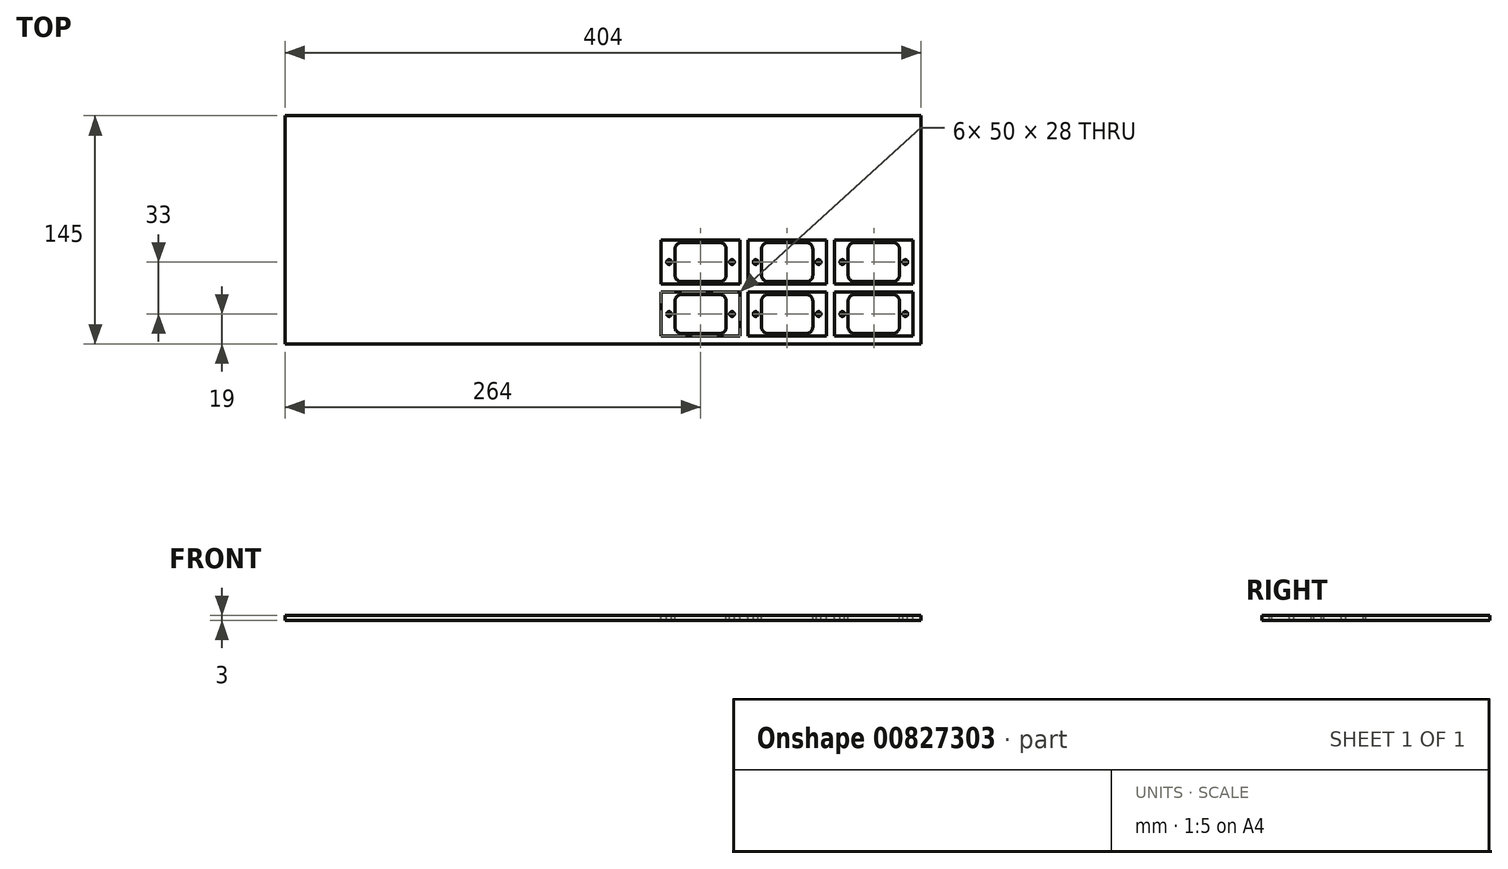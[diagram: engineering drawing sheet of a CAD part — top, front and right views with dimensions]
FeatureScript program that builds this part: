
annotation { "Feature Type Name" : "Feature", "Feature Type Description" : "" }
export const myFeature = defineFeature(function(context is Context, id is Id, definition is map)
    precondition{}
    {
        {
            var Q0;
            Q0=qCreatedBy(makeId("Top.planeOp"),FACE);
            var sketch = newSketch(context, id + "F0", { "sketchPlane" : qUnion([Q0])});
            skLineSegment(sketch, "E0.bottom", {"start": v(202, 72.5) * mm, "end": v(-202, 72.5) * mm});
            skLineSegment(sketch, "E0.top", {"start": v(202, -72.5) * mm, "end": v(-202, -72.5) * mm});
            skLineSegment(sketch, "E0.left", {"start": v(202, 72.5) * mm, "end": v(202, -72.5) * mm});
            skLineSegment(sketch, "E0.right", {"start": v(-202, 72.5) * mm, "end": v(-202, -72.5) * mm});
            skPoint(sketch, "E0.middle", {"position": v(0, 0) * mm});
            skSolve(sketch);
        }
        {
            var Q0;
            Q0=qCreatedBy(makeId("Top.planeOp"),FACE);
            var sketch = newSketch(context, id + "F1", { "sketchPlane" : qUnion([Q0])});
            skLineSegment(sketch, "E1.bottom", {"start": v(184.25, -65.9) * mm, "end": v(159.75, -65.9) * mm});
            skLineSegment(sketch, "E1.top", {"start": v(184.25, -41.1) * mm, "end": v(159.75, -41.1) * mm});
            skLineSegment(sketch, "E1.left", {"start": v(188.25, -61.9) * mm, "end": v(188.25, -45.1) * mm});
            skLineSegment(sketch, "E1.right", {"start": v(155.75, -61.9) * mm, "end": v(155.75, -45.1) * mm});
            skPoint(sketch, "E1.middle", {"position": v(172, -53.5) * mm});
            skPoint(sketch, "E2.visualSharp", {"position": v(155.75, -41.1) * mm});
            skArc(sketch, "E2.filletArc", {"start": v(159.75, -41.1) * mm, "mid": v(156.92, -42.27) * mm, "end": v(155.75, -45.1) * mm});
            skPoint(sketch, "E3.visualSharp", {"position": v(188.25, -41.1) * mm});
            skArc(sketch, "E3.filletArc", {"start": v(188.25, -45.1) * mm, "mid": v(187.08, -42.27) * mm, "end": v(184.25, -41.1) * mm});
            skPoint(sketch, "E4.visualSharp", {"position": v(188.25, -65.9) * mm});
            skArc(sketch, "E4.filletArc", {"start": v(184.25, -65.9) * mm, "mid": v(187.08, -64.73) * mm, "end": v(188.25, -61.9) * mm});
            skPoint(sketch, "E5.visualSharp", {"position": v(155.75, -65.9) * mm});
            skArc(sketch, "E5.filletArc", {"start": v(155.75, -61.9) * mm, "mid": v(156.92, -64.73) * mm, "end": v(159.75, -65.9) * mm});
            skCircle(sketch, "E6", {"center": v(192, -53.5) * mm, "radius": 1.5 * mm});
            skCircle(sketch, "E7", {"center": v(152, -53.5) * mm, "radius": 1.5 * mm});
            skLineSegment(sketch, "E8", {"start": v(147, -39.5) * mm, "end": v(147, -67.5) * mm});
            skLineSegment(sketch, "E9", {"start": v(147, -67.5) * mm, "end": v(197, -67.5) * mm});
            skLineSegment(sketch, "E10", {"start": v(197, -67.5) * mm, "end": v(197, -39.5) * mm});
            skLineSegment(sketch, "E11", {"start": v(197, -39.5) * mm, "end": v(147, -39.5) * mm});
            skLineSegment(sketch, "E12.0.1.0", {"start": v(184.25, -32.9) * mm, "end": v(159.75, -32.9) * mm});
            skLineSegment(sketch, "E12.0.1.1", {"start": v(184.25, -8.1) * mm, "end": v(159.75, -8.1) * mm});
            skLineSegment(sketch, "E12.0.1.2", {"start": v(188.25, -28.9) * mm, "end": v(188.25, -12.1) * mm});
            skPoint(sketch, "E12.0.1.3", {"position": v(155.75, -8.1) * mm});
            skLineSegment(sketch, "E12.0.1.4", {"start": v(147, -6.5) * mm, "end": v(147, -34.5) * mm});
            skPoint(sketch, "E12.0.1.5", {"position": v(188.25, -8.1) * mm});
            skPoint(sketch, "E12.0.1.6", {"position": v(188.25, -32.9) * mm});
            skLineSegment(sketch, "E12.0.1.7", {"start": v(155.75, -28.9) * mm, "end": v(155.75, -12.1) * mm});
            skPoint(sketch, "E12.0.1.8", {"position": v(172, -20.5) * mm});
            skLineSegment(sketch, "E12.0.1.9", {"start": v(197, -34.5) * mm, "end": v(197, -6.5) * mm});
            skLineSegment(sketch, "E12.0.1.10", {"start": v(147, -34.5) * mm, "end": v(197, -34.5) * mm});
            skLineSegment(sketch, "E12.0.1.11", {"start": v(197, -6.5) * mm, "end": v(147, -6.5) * mm});
            skPoint(sketch, "E12.0.1.12", {"position": v(155.75, -32.9) * mm});
            skCircle(sketch, "E12.0.1.13", {"center": v(152, -20.5) * mm, "radius": 1.5 * mm});
            skArc(sketch, "E12.0.1.14", {"start": v(188.25, -12.1) * mm, "mid": v(187.08, -9.27) * mm, "end": v(184.25, -8.1) * mm});
            skArc(sketch, "E12.0.1.15", {"start": v(184.25, -32.9) * mm, "mid": v(187.08, -31.73) * mm, "end": v(188.25, -28.9) * mm});
            skArc(sketch, "E12.0.1.16", {"start": v(155.75, -28.9) * mm, "mid": v(156.92, -31.73) * mm, "end": v(159.75, -32.9) * mm});
            skCircle(sketch, "E12.0.1.17", {"center": v(192, -20.5) * mm, "radius": 1.5 * mm});
            skArc(sketch, "E12.0.1.18", {"start": v(159.75, -8.1) * mm, "mid": v(156.92, -9.27) * mm, "end": v(155.75, -12.1) * mm});
            skLineSegment(sketch, "E12.1.0.0", {"start": v(129.25, -65.9) * mm, "end": v(104.75, -65.9) * mm});
            skLineSegment(sketch, "E12.1.0.1", {"start": v(129.25, -41.1) * mm, "end": v(104.75, -41.1) * mm});
            skLineSegment(sketch, "E12.1.0.2", {"start": v(133.25, -61.9) * mm, "end": v(133.25, -45.1) * mm});
            skPoint(sketch, "E12.1.0.3", {"position": v(100.75, -41.1) * mm});
            skLineSegment(sketch, "E12.1.0.4", {"start": v(92, -39.5) * mm, "end": v(92, -67.5) * mm});
            skPoint(sketch, "E12.1.0.5", {"position": v(133.25, -41.1) * mm});
            skPoint(sketch, "E12.1.0.6", {"position": v(133.25, -65.9) * mm});
            skLineSegment(sketch, "E12.1.0.7", {"start": v(100.75, -61.9) * mm, "end": v(100.75, -45.1) * mm});
            skPoint(sketch, "E12.1.0.8", {"position": v(117, -53.5) * mm});
            skLineSegment(sketch, "E12.1.0.9", {"start": v(142, -67.5) * mm, "end": v(142, -39.5) * mm});
            skLineSegment(sketch, "E12.1.0.10", {"start": v(92, -67.5) * mm, "end": v(142, -67.5) * mm});
            skLineSegment(sketch, "E12.1.0.11", {"start": v(142, -39.5) * mm, "end": v(92, -39.5) * mm});
            skPoint(sketch, "E12.1.0.12", {"position": v(100.75, -65.9) * mm});
            skCircle(sketch, "E12.1.0.13", {"center": v(97, -53.5) * mm, "radius": 1.5 * mm});
            skArc(sketch, "E12.1.0.14", {"start": v(133.25, -45.1) * mm, "mid": v(132.08, -42.27) * mm, "end": v(129.25, -41.1) * mm});
            skArc(sketch, "E12.1.0.15", {"start": v(129.25, -65.9) * mm, "mid": v(132.08, -64.73) * mm, "end": v(133.25, -61.9) * mm});
            skArc(sketch, "E12.1.0.16", {"start": v(100.75, -61.9) * mm, "mid": v(101.92, -64.73) * mm, "end": v(104.75, -65.9) * mm});
            skCircle(sketch, "E12.1.0.17", {"center": v(137, -53.5) * mm, "radius": 1.5 * mm});
            skArc(sketch, "E12.1.0.18", {"start": v(104.75, -41.1) * mm, "mid": v(101.92, -42.27) * mm, "end": v(100.75, -45.1) * mm});
            skLineSegment(sketch, "E12.1.1.0", {"start": v(129.25, -32.9) * mm, "end": v(104.75, -32.9) * mm});
            skLineSegment(sketch, "E12.1.1.1", {"start": v(129.25, -8.1) * mm, "end": v(104.75, -8.1) * mm});
            skLineSegment(sketch, "E12.1.1.2", {"start": v(133.25, -28.9) * mm, "end": v(133.25, -12.1) * mm});
            skPoint(sketch, "E12.1.1.3", {"position": v(100.75, -8.1) * mm});
            skLineSegment(sketch, "E12.1.1.4", {"start": v(92, -6.5) * mm, "end": v(92, -34.5) * mm});
            skPoint(sketch, "E12.1.1.5", {"position": v(133.25, -8.1) * mm});
            skPoint(sketch, "E12.1.1.6", {"position": v(133.25, -32.9) * mm});
            skLineSegment(sketch, "E12.1.1.7", {"start": v(100.75, -28.9) * mm, "end": v(100.75, -12.1) * mm});
            skPoint(sketch, "E12.1.1.8", {"position": v(117, -20.5) * mm});
            skLineSegment(sketch, "E12.1.1.9", {"start": v(142, -34.5) * mm, "end": v(142, -6.5) * mm});
            skLineSegment(sketch, "E12.1.1.10", {"start": v(92, -34.5) * mm, "end": v(142, -34.5) * mm});
            skLineSegment(sketch, "E12.1.1.11", {"start": v(142, -6.5) * mm, "end": v(92, -6.5) * mm});
            skPoint(sketch, "E12.1.1.12", {"position": v(100.75, -32.9) * mm});
            skCircle(sketch, "E12.1.1.13", {"center": v(97, -20.5) * mm, "radius": 1.5 * mm});
            skArc(sketch, "E12.1.1.14", {"start": v(133.25, -12.1) * mm, "mid": v(132.08, -9.27) * mm, "end": v(129.25, -8.1) * mm});
            skArc(sketch, "E12.1.1.15", {"start": v(129.25, -32.9) * mm, "mid": v(132.08, -31.73) * mm, "end": v(133.25, -28.9) * mm});
            skArc(sketch, "E12.1.1.16", {"start": v(100.75, -28.9) * mm, "mid": v(101.92, -31.73) * mm, "end": v(104.75, -32.9) * mm});
            skCircle(sketch, "E12.1.1.17", {"center": v(137, -20.5) * mm, "radius": 1.5 * mm});
            skArc(sketch, "E12.1.1.18", {"start": v(104.75, -8.1) * mm, "mid": v(101.92, -9.27) * mm, "end": v(100.75, -12.1) * mm});
            skLineSegment(sketch, "E12.2.0.0", {"start": v(74.25, -65.9) * mm, "end": v(49.75, -65.9) * mm});
            skLineSegment(sketch, "E12.2.0.1", {"start": v(74.25, -41.1) * mm, "end": v(49.75, -41.1) * mm});
            skLineSegment(sketch, "E12.2.0.2", {"start": v(78.25, -61.9) * mm, "end": v(78.25, -45.1) * mm});
            skPoint(sketch, "E12.2.0.3", {"position": v(45.75, -41.1) * mm});
            skLineSegment(sketch, "E12.2.0.4", {"start": v(37, -39.5) * mm, "end": v(37, -67.5) * mm});
            skPoint(sketch, "E12.2.0.5", {"position": v(78.25, -41.1) * mm});
            skPoint(sketch, "E12.2.0.6", {"position": v(78.25, -65.9) * mm});
            skLineSegment(sketch, "E12.2.0.7", {"start": v(45.75, -61.9) * mm, "end": v(45.75, -45.1) * mm});
            skPoint(sketch, "E12.2.0.8", {"position": v(62, -53.5) * mm});
            skLineSegment(sketch, "E12.2.0.9", {"start": v(87, -67.5) * mm, "end": v(87, -39.5) * mm});
            skLineSegment(sketch, "E12.2.0.10", {"start": v(37, -67.5) * mm, "end": v(87, -67.5) * mm});
            skLineSegment(sketch, "E12.2.0.11", {"start": v(87, -39.5) * mm, "end": v(37, -39.5) * mm});
            skPoint(sketch, "E12.2.0.12", {"position": v(45.75, -65.9) * mm});
            skCircle(sketch, "E12.2.0.13", {"center": v(42, -53.5) * mm, "radius": 1.5 * mm});
            skArc(sketch, "E12.2.0.14", {"start": v(78.25, -45.1) * mm, "mid": v(77.08, -42.27) * mm, "end": v(74.25, -41.1) * mm});
            skArc(sketch, "E12.2.0.15", {"start": v(74.25, -65.9) * mm, "mid": v(77.08, -64.73) * mm, "end": v(78.25, -61.9) * mm});
            skArc(sketch, "E12.2.0.16", {"start": v(45.75, -61.9) * mm, "mid": v(46.92, -64.73) * mm, "end": v(49.75, -65.9) * mm});
            skCircle(sketch, "E12.2.0.17", {"center": v(82, -53.5) * mm, "radius": 1.5 * mm});
            skArc(sketch, "E12.2.0.18", {"start": v(49.75, -41.1) * mm, "mid": v(46.92, -42.27) * mm, "end": v(45.75, -45.1) * mm});
            skLineSegment(sketch, "E12.2.1.0", {"start": v(74.25, -32.9) * mm, "end": v(49.75, -32.9) * mm});
            skLineSegment(sketch, "E12.2.1.1", {"start": v(74.25, -8.1) * mm, "end": v(49.75, -8.1) * mm});
            skLineSegment(sketch, "E12.2.1.2", {"start": v(78.25, -28.9) * mm, "end": v(78.25, -12.1) * mm});
            skPoint(sketch, "E12.2.1.3", {"position": v(45.75, -8.1) * mm});
            skLineSegment(sketch, "E12.2.1.4", {"start": v(37, -6.5) * mm, "end": v(37, -34.5) * mm});
            skPoint(sketch, "E12.2.1.5", {"position": v(78.25, -8.1) * mm});
            skPoint(sketch, "E12.2.1.6", {"position": v(78.25, -32.9) * mm});
            skLineSegment(sketch, "E12.2.1.7", {"start": v(45.75, -28.9) * mm, "end": v(45.75, -12.1) * mm});
            skPoint(sketch, "E12.2.1.8", {"position": v(62, -20.5) * mm});
            skLineSegment(sketch, "E12.2.1.9", {"start": v(87, -34.5) * mm, "end": v(87, -6.5) * mm});
            skLineSegment(sketch, "E12.2.1.10", {"start": v(37, -34.5) * mm, "end": v(87, -34.5) * mm});
            skLineSegment(sketch, "E12.2.1.11", {"start": v(87, -6.5) * mm, "end": v(37, -6.5) * mm});
            skPoint(sketch, "E12.2.1.12", {"position": v(45.75, -32.9) * mm});
            skCircle(sketch, "E12.2.1.13", {"center": v(42, -20.5) * mm, "radius": 1.5 * mm});
            skArc(sketch, "E12.2.1.14", {"start": v(78.25, -12.1) * mm, "mid": v(77.08, -9.27) * mm, "end": v(74.25, -8.1) * mm});
            skArc(sketch, "E12.2.1.15", {"start": v(74.25, -32.9) * mm, "mid": v(77.08, -31.73) * mm, "end": v(78.25, -28.9) * mm});
            skArc(sketch, "E12.2.1.16", {"start": v(45.75, -28.9) * mm, "mid": v(46.92, -31.73) * mm, "end": v(49.75, -32.9) * mm});
            skCircle(sketch, "E12.2.1.17", {"center": v(82, -20.5) * mm, "radius": 1.5 * mm});
            skArc(sketch, "E12.2.1.18", {"start": v(49.75, -8.1) * mm, "mid": v(46.92, -9.27) * mm, "end": v(45.75, -12.1) * mm});
            skLineSegment(sketch, "E12.direction1", {"start": v(147, -67.5) * mm, "end": v(92, -67.5) * mm});
            skLineSegment(sketch, "E12.direction2", {"start": v(147, -67.5) * mm, "end": v(147, -34.5) * mm});
            skSolve(sketch);
        }
        {
            var Q0;
            Q0=makeQuery(id+"F0.imprint","IMPRINT",FACE,{"disambiguationData":[TD([[makeQuery(id+"F0.imprint","IMPRINT",EDGE,{"derivedFrom":sQuery(id+"F0.wireOp",EDGE,"E0.bottom")}),1.0]])]});
            extrude(context, id + "F2", {"entities" : qUnion([Q0]), "oppositeDirection" : true, "depth" : 3 * mm, "offsetDistance" : 25 * mm});
        }
        {
            var Q0;
            Q0 = qSketchRegion(id + "F1", true);
            var Q1;
            Q1=makeQuery(id+"F2.opExtrude","CAP_FACE",FACE,{"disambiguationData":[OSD([sQuery(id+"F0.wireOp",EDGE,"E0.bottom"),sQuery(id+"F0.wireOp",EDGE,"E0.top"),sQuery(id+"F0.wireOp",EDGE,"E0.left"),sQuery(id+"F0.wireOp",EDGE,"E0.right")])],"isStart":false});
            extrude(context, id + "F3", {"entities" : qUnion([Q0]), "operationType" : NewBodyOperationType.REMOVE, "endBound" : BoundingType.UP_TO_SURFACE, "oppositeDirection" : true, "depth" : 25 * mm, "endBoundEntityFace" : qUnion([Q1]), "offsetDistance" : 25 * mm});
        }
    });
